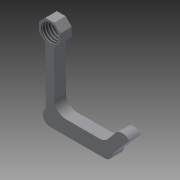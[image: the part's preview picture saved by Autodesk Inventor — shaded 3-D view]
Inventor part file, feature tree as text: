
AUTODESK INVENTOR PART (.ipt)
format: ipt  version: 2015 SP2 (Build 190223200, 223)  size: 137,216 bytes
history: native  units: mm
features: sketch x15, extrude x6, plane x5, fillet x3, hole x1, thread x1
ambient origin geometry x8: Origin, YZ Plane, XZ Plane, XY Plane, X Axis, Y Axis, Z Axis, Center Point
bodies: Solid1 (feature_tree)
feature tree (31):
  sketch  "Sketch1"  dims[d4=2.0mm d5=0.0mm d6=10.0mm d7=0.0mm]
  sketch  "Sketch2"  dims[d10=2.0mm d11=0.0mm d15=2.0mm d16=0.0mm]
  plane  "Work Plane1"
  extrude  "Extrusion2"  Depth=10.0mm TaperAngle=0.0deg
  plane  "Work Plane2"
  extrude  "Extrusion3"  Depth=2.0mm TaperAngle=0.0deg
  sketch  "Sketch5"  dims[d24=3.0mm d25=6.0mm d26=4.0mm d27=2.0mm d28=90.0deg d29=8.0mm d30=20.594885mm d31=10.0mm d32=0.0mm]
  sketch  "Sketch6"  dims[d33=2.0mm d34=2.0mm]
  extrude  "Extrusion4"  Depth=2.0mm TaperAngle=0.0deg
  sketch  "Sketch8"
  sketch  "Sketch9"
  sketch  "Sketch11"
  sketch  "Sketch12"
  plane  "Work Plane3"
  extrude  "Extrusion6"  Depth=2.0mm TaperAngle=0.0deg
  plane  "Work Plane4"
  extrude  "Extrusion7"  Depth=10.0mm TaperAngle=0.0deg
  plane  "Work Plane5"
  extrude  "Extrusion8"  Depth=2.0mm
  sketch  "Sketch16"
  hole  "Hole1"  [1 undecoded]
  thread  "Thread2"  [1 undecoded]
  fillet  "Fillet1"  [1 undecoded]
  fillet  "Fillet2"  [1 undecoded]
  fillet  "Fillet3"  [1 undecoded]
  sketch  "Sketch3"  dims[d17=2.483mm d18=2.0mm d19=0.0mm]
  sketch  "Sketch4"  dims[d20=8.726646mm d21=2.0mm d22=0.0mm]
  sketch  "Sketch7"  dims[d35=2.0mm]
  sketch  "Sketch13"
  sketch  "Sketch14"
  sketch  "Sketch15"
note: 5 required parameter values undecoded (feature->parameter linkage not recoverable at this tier; creation-order binding heuristic only, values carry confidence <= 0.55)
